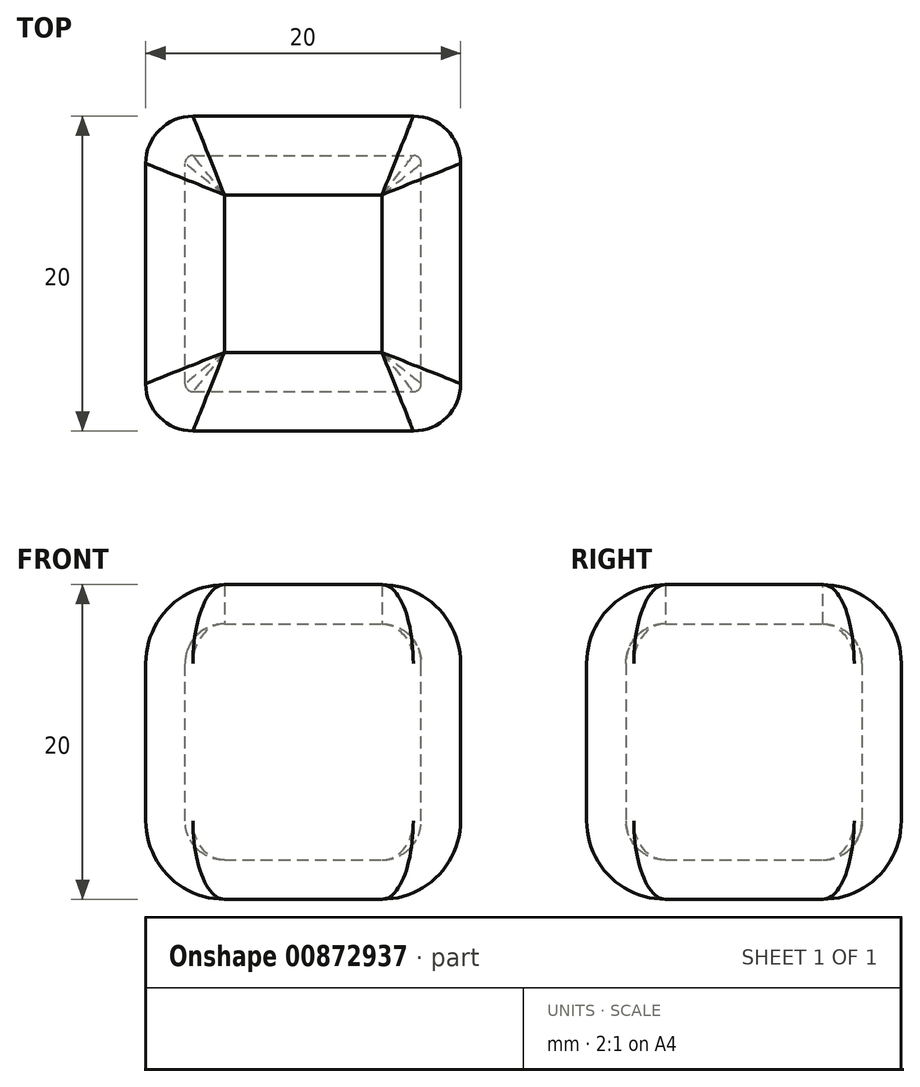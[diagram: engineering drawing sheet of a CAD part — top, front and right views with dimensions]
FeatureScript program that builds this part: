
annotation { "Feature Type Name" : "Feature", "Feature Type Description" : "" }
export const myFeature = defineFeature(function(context is Context, id is Id, definition is map)
    precondition{}
    {
        {
            var Q0;
            Q0=qCreatedBy(makeId("Top.planeOp"),FACE);
            var sketch = newSketch(context, id + "F0", { "sketchPlane" : qUnion([Q0])});
            skLineSegment(sketch, "E0.bottom", {"start": v(7, -10) * mm, "end": v(-7, -10) * mm});
            skLineSegment(sketch, "E0.top", {"start": v(7, 10) * mm, "end": v(-7, 10) * mm});
            skLineSegment(sketch, "E0.left", {"start": v(10, -7) * mm, "end": v(10, 7) * mm});
            skLineSegment(sketch, "E0.right", {"start": v(-10, -7) * mm, "end": v(-10, 7) * mm});
            skPoint(sketch, "E0.middle", {"position": v(0, 0) * mm});
            skPoint(sketch, "E1.visualSharp", {"position": v(-10, 10) * mm});
            skArc(sketch, "E1.filletArc", {"start": v(-7, 10) * mm, "mid": v(-9.12, 9.12) * mm, "end": v(-10, 7) * mm});
            skPoint(sketch, "E2.visualSharp", {"position": v(10, 10) * mm});
            skArc(sketch, "E2.filletArc", {"start": v(10, 7) * mm, "mid": v(9.12, 9.12) * mm, "end": v(7, 10) * mm});
            skPoint(sketch, "E3.visualSharp", {"position": v(10, -10) * mm});
            skArc(sketch, "E3.filletArc", {"start": v(7, -10) * mm, "mid": v(9.12, -9.12) * mm, "end": v(10, -7) * mm});
            skPoint(sketch, "E4.visualSharp", {"position": v(-10, -10) * mm});
            skArc(sketch, "E4.filletArc", {"start": v(-10, -7) * mm, "mid": v(-9.12, -9.12) * mm, "end": v(-7, -10) * mm});
            skSolve(sketch);
        }
        {
            var Q0;
            Q0=makeQuery(id+"F0.imprint","IMPRINT",FACE,{"disambiguationData":[TD([[makeQuery(id+"F0.imprint","IMPRINT",EDGE,{"derivedFrom":sQuery(id+"F0.wireOp",EDGE,"E0.bottom")}),-1.0]])]});
            extrude(context, id + "F1", {"entities" : qUnion([Q0]), "depth" : 20 * mm, "offsetDistance" : 25 * mm});
        }
        {
            var Q0;
            Q0=makeQuery(id+"F1.opExtrude","CAP_EDGE",EDGE,{"disambiguationData":[OSD([sQuery(id+"F0.wireOp",EDGE,"E0.bottom")])],"isStart":false});
            var Q1;
            Q1=makeQuery(id+"F1.opExtrude","CAP_EDGE",EDGE,{"disambiguationData":[OSD([sQuery(id+"F0.wireOp",EDGE,"E0.left")])],"isStart":true});
            fillet(context, id + "F2", {"entities" : qUnion([Q0, Q1]), "radius" : 5 * mm, "tangentPropagation" : true, "allowEdgeOverflow" : false});
        }
        {
            var Q0;
            Q0=makeQuery(id+"F1.opExtrude","CAP_FACE",FACE,{"disambiguationData":[OSD([sQuery(id+"F0.wireOp",EDGE,"E0.bottom"),sQuery(id+"F0.wireOp",EDGE,"E0.top"),sQuery(id+"F0.wireOp",EDGE,"E0.left"),sQuery(id+"F0.wireOp",EDGE,"E0.right"),sQuery(id+"F0.wireOp",EDGE,"E1.filletArc"),sQuery(id+"F0.wireOp",EDGE,"E2.filletArc"),sQuery(id+"F0.wireOp",EDGE,"E3.filletArc"),sQuery(id+"F0.wireOp",EDGE,"E4.filletArc")])],"isStart":false});
            shell(context, id + "F3", {"entities" : qUnion([Q0]), "thickness" : 2.5 * mm});
        }
    });
